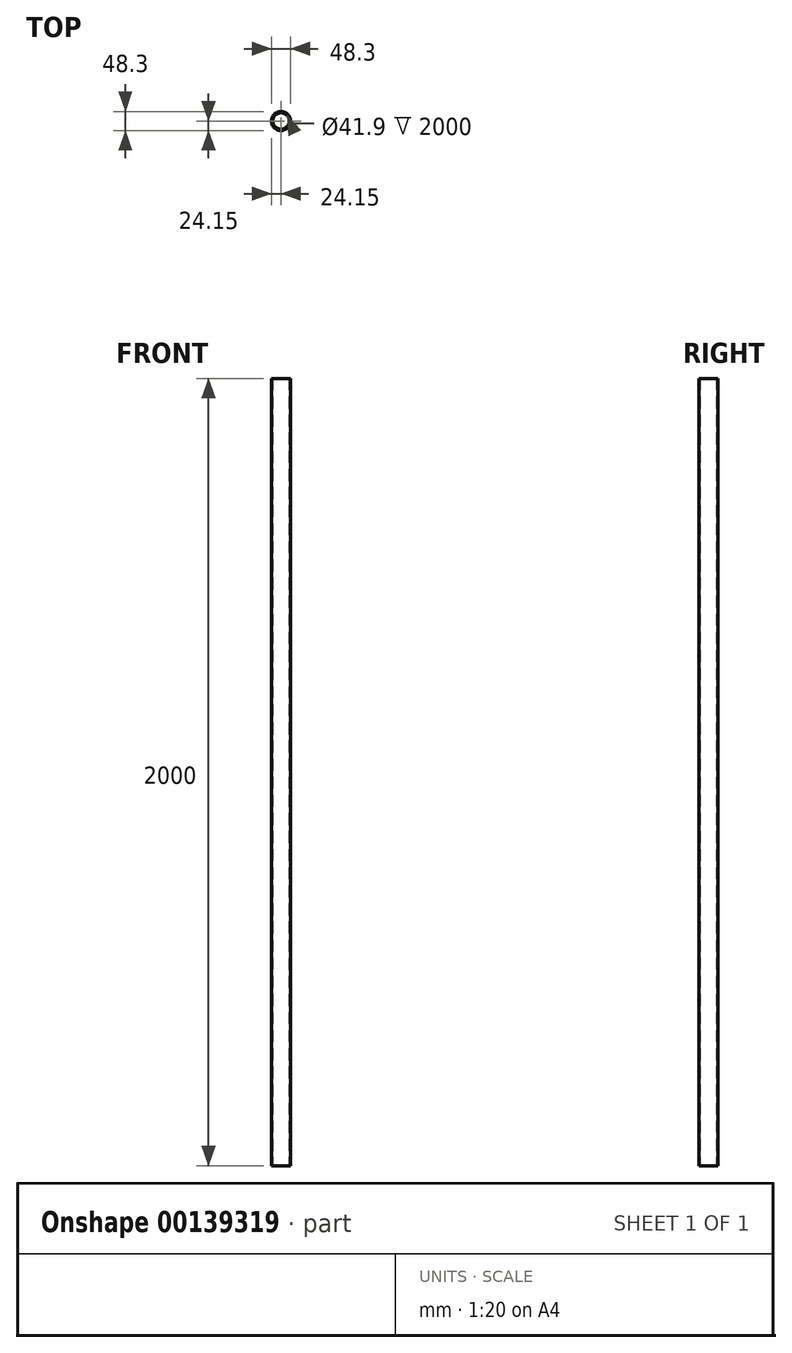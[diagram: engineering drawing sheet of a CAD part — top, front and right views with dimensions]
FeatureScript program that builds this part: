
annotation { "Feature Type Name" : "Feature", "Feature Type Description" : "" }
export const myFeature = defineFeature(function(context is Context, id is Id, definition is map)
    precondition{}
    {
        {
            var Q0;
            Q0=qCreatedBy(makeId("Top.planeOp"),FACE);
            var sketch = newSketch(context, id + "F0", { "sketchPlane" : qUnion([Q0])});
            skCircle(sketch, "E0", {"center": v(0, 0) * mm, "radius": 24.15 * mm});
            skCircle(sketch, "E1", {"center": v(0, 0) * mm, "radius": 20.95 * mm});
            skSolve(sketch);
        }
        {
            var Q0;
            Q0 = qSketchRegion(id + "F0", true);
            extrude(context, id + "F1", {"entities" : qUnion([Q0]), "depth" : 2000 * mm});
        }
    });
